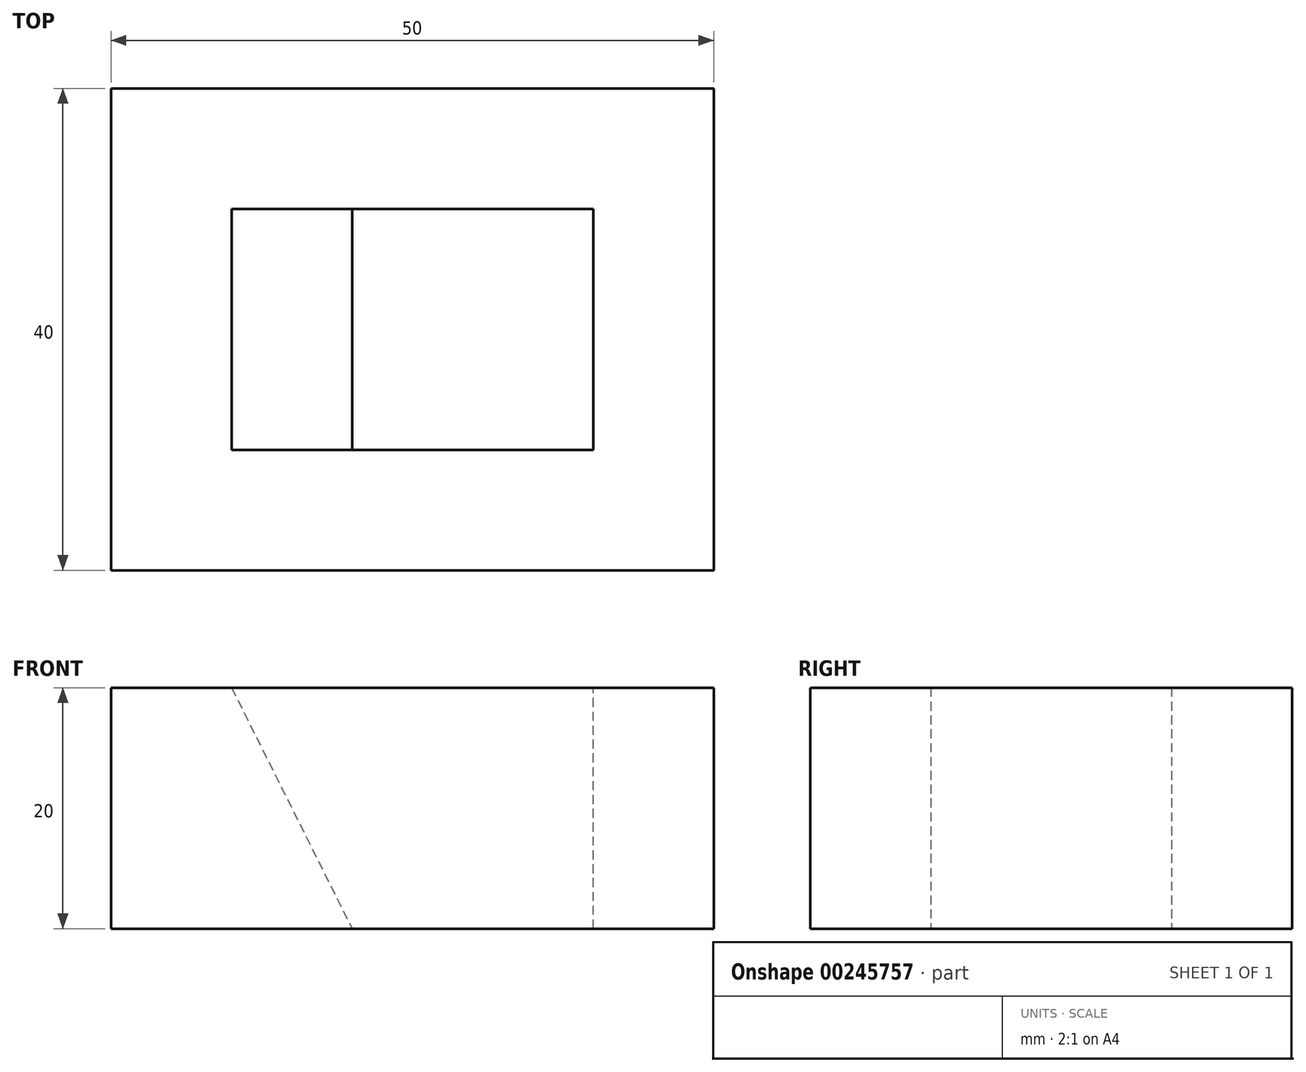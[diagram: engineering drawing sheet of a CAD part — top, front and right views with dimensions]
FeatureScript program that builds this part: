
annotation { "Feature Type Name" : "Feature", "Feature Type Description" : "" }
export const myFeature = defineFeature(function(context is Context, id is Id, definition is map)
    precondition{}
    {
        {
            var Q0;
            Q0=qCreatedBy(makeId("Top.planeOp"),FACE);
            var sketch = newSketch(context, id + "F0", { "sketchPlane" : qUnion([Q0])});
            skLineSegment(sketch, "E0.bottom", {"start": v(0, 0) * mm, "end": v(50, 0) * mm});
            skLineSegment(sketch, "E0.top", {"start": v(0, 40) * mm, "end": v(50, 40) * mm});
            skLineSegment(sketch, "E0.left", {"start": v(0, 0) * mm, "end": v(0, 40) * mm});
            skLineSegment(sketch, "E0.right", {"start": v(50, 0) * mm, "end": v(50, 40) * mm});
            skSolve(sketch);
        }
        {
            var Q0;
            Q0=makeQuery(id+"F0.imprint","IMPRINT",FACE,{"disambiguationData":[TD([[makeQuery(id+"F0.imprint","IMPRINT",EDGE,{"derivedFrom":sQuery(id+"F0.wireOp",EDGE,"E0.bottom")}),1.0]])]});
            extrude(context, id + "F1", {"entities" : qUnion([Q0]), "depth" : 20 * mm});
        }
        {
            var Q0;
            Q0=makeQuery(id+"F1.opExtrude","CAP_FACE",FACE,{"disambiguationData":[OSD([sQuery(id+"F0.wireOp",EDGE,"E0.bottom"),sQuery(id+"F0.wireOp",EDGE,"E0.top"),sQuery(id+"F0.wireOp",EDGE,"E0.left"),sQuery(id+"F0.wireOp",EDGE,"E0.right")])],"isStart":false});
            var sketch = newSketch(context, id + "F2", { "sketchPlane" : qUnion([Q0])});
            skLineSegment(sketch, "E1.bottom", {"start": v(10, 10) * mm, "end": v(40, 10) * mm});
            skLineSegment(sketch, "E1.top", {"start": v(10, 30) * mm, "end": v(40, 30) * mm});
            skLineSegment(sketch, "E1.left", {"start": v(10, 10) * mm, "end": v(10, 30) * mm});
            skLineSegment(sketch, "E1.right", {"start": v(40, 10) * mm, "end": v(40, 30) * mm});
            skSolve(sketch);
        }
        {
            var Q0;
            Q0=makeQuery(id+"F2.imprint","IMPRINT",FACE,{"disambiguationData":[TD([[makeQuery(id+"F2.imprint","IMPRINT",EDGE,{"derivedFrom":sQuery(id+"F2.wireOp",EDGE,"E1.bottom")}),1.0]])]});
            extrude(context, id + "F3", {"entities" : qUnion([Q0]), "operationType" : NewBodyOperationType.REMOVE, "oppositeDirection" : true, "depth" : 20 * mm});
        }
        {
            var Q0;
            Q0=makeQuery(id+"F3.boolean.opBoolean","COPY",FACE,{"derivedFrom":makeQuery(id+"F3.opExtrude","SWEPT_FACE",FACE,{"disambiguationData":[OSD([sQuery(id+"F2.wireOp",EDGE,"E1.top")])]})});
            var sketch = newSketch(context, id + "F4", { "sketchPlane" : qUnion([Q0])});
            skLineSegment(sketch, "E2", {"start": v(10, 20) * mm, "end": v(20, 0) * mm});
            skSolve(sketch);
        }
        {
            var Q0;
            {var subQ0=sQuery(id+"F4.wireOp",EDGE,"E2");Q0=makeQuery(id+"F4.imprint","IMPRINT",FACE,{"disambiguationData":[TD([[makeQuery(id+"F4.imprint","IMPRINT",EDGE,{"derivedFrom":subQ0}),-1.0]])]});}
            extrude(context, id + "F5", {"entities" : qUnion([Q0]), "operationType" : NewBodyOperationType.ADD, "depth" : 20 * mm});
        }
    });
